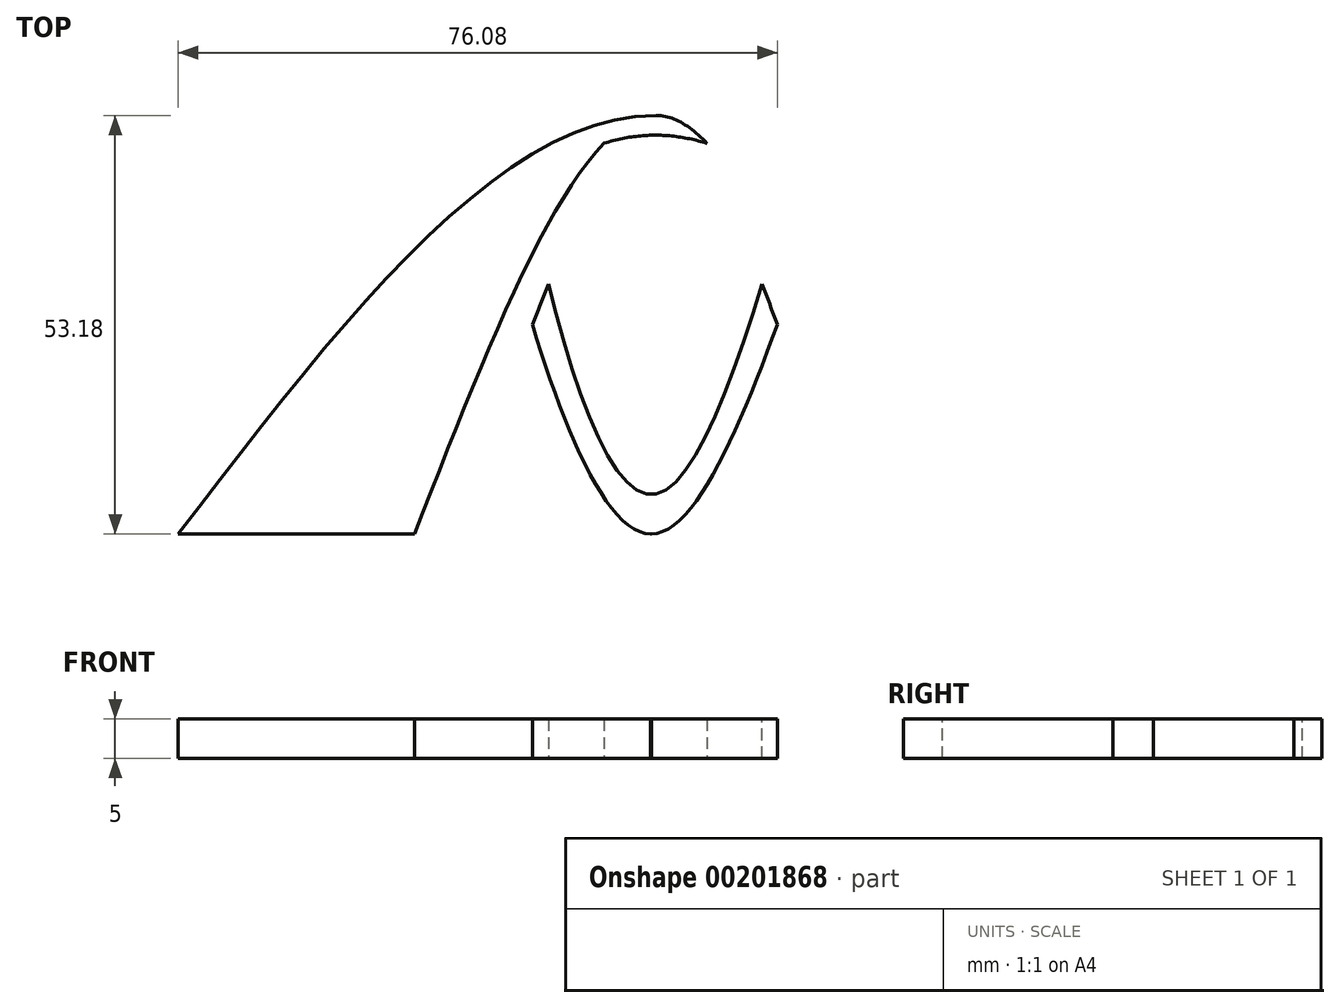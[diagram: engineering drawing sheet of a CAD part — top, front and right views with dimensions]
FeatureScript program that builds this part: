
annotation { "Feature Type Name" : "Feature", "Feature Type Description" : "" }
export const myFeature = defineFeature(function(context is Context, id is Id, definition is map)
    precondition{}
    {
        {
            var Q0;
            Q0=qCreatedBy(makeId("Top.planeOp"),FACE);
            var sketch = newSketch(context, id + "F0", { "sketchPlane" : qUnion([Q0])});
            skLineSegment(sketch, "E0", {"start": v(-37.54, -3.3) * mm, "end": v(82.46, -3.3) * mm});
            skLineSegment(sketch, "E1", {"start": v(82.46, -3.3) * mm, "end": v(77.46, -3.3) * mm});
            skLineSegment(sketch, "E2", {"start": v(23.2, 49.88) * mm, "end": v(23.2, 47.38) * mm});
            skLineSegment(sketch, "E3", {"start": v(52.36, -3.3) * mm, "end": v(52.36, 24.25) * mm, "construction": true});
            skLineSegment(sketch, "E4.MirrorCS", {"start": v(-7.54, -3.3) * mm, "end": v(-1.75, -3.3) * mm});
            skLineSegment(sketch, "E5", {"start": v(22.46, -3.3) * mm, "end": v(22.46, 1.7) * mm, "construction": true});
            skLineSegment(sketch, "E6", {"start": v(36.6, 28.45) * mm, "end": v(9.47, 28.45) * mm, "construction": true});
            skLineSegment(sketch, "E7", {"start": v(38.54, 23.33) * mm, "end": v(7.45, 23.33) * mm, "construction": true});
            skFitSpline(sketch, "E8", {"points": [v(9.47, 28.45) * mm, v(22.46, 1.7) * mm, v(36.6, 28.45) * mm], "startDerivative": vector(21.29, -87.77) * mm, "endDerivative": vector(26.63, 87.43) * mm});
            skFitSpline(sketch, "E9", {"points": [v(38.54, 23.33) * mm, v(22.46, -3.3) * mm, v(7.45, 23.33) * mm], "startDerivative": vector(-29.76, -81.8) * mm, "endDerivative": vector(-24.63, 82.18) * mm});
            skLineSegment(sketch, "E10", {"start": v(-7.54, -3.3) * mm, "end": v(-7.54, 19.7) * mm, "construction": true});
            skLineSegment(sketch, "E11", {"start": v(-7.54, 19.7) * mm, "end": v(-1.75, -3.3) * mm, "construction": true});
            skLineSegment(sketch, "E12", {"start": v(-1.75, -3.3) * mm, "end": v(-1.75, 19.7) * mm, "construction": true});
            skLineSegment(sketch, "E13", {"start": v(-1.75, 19.7) * mm, "end": v(-7.54, -3.3) * mm, "construction": true});
            skLineSegment(sketch, "E14", {"start": v(47.36, -3.3) * mm, "end": v(47.36, 24.25) * mm, "construction": true});
            skLineSegment(sketch, "E15", {"start": v(-37.54, -3.3) * mm, "end": v(-37.54, 18.32) * mm, "construction": true});
            skLineSegment(sketch, "E16", {"start": v(-32.54, -3.3) * mm, "end": v(-32.54, 18.32) * mm, "construction": true});
            skLineSegment(sketch, "E17", {"start": v(77.46, -3.3) * mm, "end": v(77.46, 15.13) * mm, "construction": true});
            skLineSegment(sketch, "E18", {"start": v(77.46, 15.13) * mm, "end": v(82.46, -3.3) * mm, "construction": true});
            skLineSegment(sketch, "E19", {"start": v(82.46, -3.3) * mm, "end": v(82.46, 15.13) * mm, "construction": true});
            skFitSpline(sketch, "E20", {"points": [v(-37.54, -3.3) * mm, v(23.2, 49.88) * mm, v(82.46, -3.3) * mm], "startDerivative": vector(121.58, 159.36) * mm, "endDerivative": vector(118.42, -159.72) * mm});
            skFitSpline(sketch, "E21", {"points": [v(77.46, -3.3) * mm, v(23.2, 47.38) * mm, v(-32.54, -3.3) * mm], "startDerivative": vector(-108.4, 152.22) * mm, "endDerivative": vector(-111.6, -151.85) * mm});
            skFitSpline(sketch, "E22", {"points": [v(-7.54, -3.3) * mm, v(23.2, 49.88) * mm, v(52.36, -3.3) * mm], "startDerivative": vector(61.97, 159.37) * mm, "endDerivative": vector(57.83, -159.7) * mm});
            skFitSpline(sketch, "E23", {"points": [v(47.36, -3.3) * mm, v(23.2, 47.38) * mm, v(-1.75, -3.3) * mm], "startDerivative": vector(-48.06, 152.11) * mm, "endDerivative": vector(-50.15, -151.96) * mm});
            skSolve(sketch);
        }
        {
            var Q0;
            {var subQ5=sQuery(id+"F0.wireOp",EDGE,"E5");Q0=makeQuery(id+"F0.imprint","IMPRINT",FACE,{"disambiguationData":[TD([[makeQuery(id+"F0.imprint","IMPRINT",EDGE,{"derivedFrom":subQ5}),-1.0]])]});}
            var Q1;
            {var subQ5=sQuery(id+"F0.wireOp",EDGE,"E5");Q1=makeQuery(id+"F0.imprint","IMPRINT",FACE,{"disambiguationData":[TD([[makeQuery(id+"F0.imprint","IMPRINT",EDGE,{"derivedFrom":subQ5}),1.0]])]});}
            var Q2;
            {var subQ1=sQuery(id+"F0.wireOp",EDGE,"E4.MirrorCS");Q2=makeQuery(id+"F0.imprint","IMPRINT",FACE,{"disambiguationData":[TD([[makeQuery(id+"F0.imprint","IMPRINT",EDGE,{"derivedFrom":subQ1}),1.0]])]});}
            var Q3;
            {var subQ1=sQuery(id+"F0.wireOp",EDGE,"OvUUgDSr-wtTh-O6yu-A5Gy-frmQIv1nZIb4");Q3=makeQuery(id+"F0.imprint","IMPRINT",FACE,{"disambiguationData":[TD([[makeQuery(id+"F0.imprint","IMPRINT",EDGE,{"derivedFrom":subQ1}),-1.0]])]});}
            var Q4;
            {var subQ0=sQuery(id+"F0.wireOp",EDGE,"E2");Q4=makeQuery(id+"F0.imprint","IMPRINT",FACE,{"disambiguationData":[TD([[makeQuery(id+"F0.imprint","IMPRINT",EDGE,{"derivedFrom":subQ0}),1.0]])]});}
            var Q5;
            {var subQ0=sQuery(id+"F0.wireOp",EDGE,"E2");Q5=makeQuery(id+"F0.imprint","IMPRINT",FACE,{"disambiguationData":[TD([[makeQuery(id+"F0.imprint","IMPRINT",EDGE,{"derivedFrom":subQ0}),-1.0]])]});}
            var Q6;
            {var subQ0=sQuery(id+"F0.wireOp",EDGE,"36bfbb2f-800a-49d8-9829-9ce1a7e19fd40.MirrorCS");Q6=makeQuery(id+"F0.imprint","IMPRINT",FACE,{"disambiguationData":[TD([[makeQuery(id+"F0.imprint","IMPRINT",EDGE,{"derivedFrom":subQ0}),1.0]])]});}
            var Q7;
            {var subQ0=sQuery(id+"F0.wireOp",EDGE,"NDid1P8x-BPUJ-Yyow-KnYY-gHr5R81uyyj0");var subQ1=sQuery(id+"F0.wireOp",EDGE,"e2933105-fd20-469f-b6d8-af79f33f81c5");var subQ2=makeQuery(id+"F0.imprint","INTERSECT",VERTEX,{"derivedFrom":[subQ1,subQ0]});Q7=makeQuery(id+"F0.imprint","IMPRINT",FACE,{"disambiguationData":[TD([[makeQuery(id+"F0.imprint","IMPRINT",EDGE,{"disambiguationData":[TD([[subQ2,-1.0]])],"derivedFrom":subQ1}),-1.0]])]});}
            var Q8;
            {var subQ0=sQuery(id+"F0.wireOp",EDGE,"E1");Q8=makeQuery(id+"F0.imprint","IMPRINT",FACE,{"disambiguationData":[TD([[makeQuery(id+"F0.imprint","IMPRINT",EDGE,{"derivedFrom":subQ0}),-1.0]])]});}
            var Q9;
            {var subQ2=sQuery(id+"F0.wireOp",EDGE,"E0");var subQ4=sQuery(id+"F0.wireOp",EDGE,"E22");var subQ5=makeQuery(id+"F0.imprint","INTERSECT",VERTEX,{"derivedFrom":[subQ2,subQ4]});Q9=makeQuery(id+"F0.imprint","IMPRINT",FACE,{"disambiguationData":[TD([[makeQuery(id+"F0.imprint","IMPRINT",EDGE,{"disambiguationData":[TD([[subQ5,1.0]])],"derivedFrom":subQ2}),1.0]])]});}
            var Q10;
            {var subQ5=sQuery(id+"F0.wireOp",EDGE,"E8");Q10=makeQuery(id+"F0.imprint","IMPRINT",FACE,{"disambiguationData":[TD([[makeQuery(id+"F0.imprint","IMPRINT",EDGE,{"derivedFrom":subQ5}),-1.0]])]});}
            var Q11;
            {var subQ0=sQuery(id+"F0.wireOp",EDGE,"E20");var subQ1=sQuery(id+"F0.wireOp",EDGE,"E0");var subQ2=makeQuery(id+"F0.imprint","INTERSECT",VERTEX,{"derivedFrom":[subQ1,subQ0]});Q11=makeQuery(id+"F0.imprint","IMPRINT",FACE,{"disambiguationData":[TD([[makeQuery(id+"F0.imprint","IMPRINT",EDGE,{"disambiguationData":[TD([[subQ2,-1.0]])],"derivedFrom":subQ1}),1.0]])]});}
            extrude(context, id + "F1", {"entities" : qUnion([Q0, Q1, Q2, Q3, Q4, Q5, Q6, Q7, Q8, Q9, Q10, Q11]), "depth" : 5 * mm});
        }
    });
